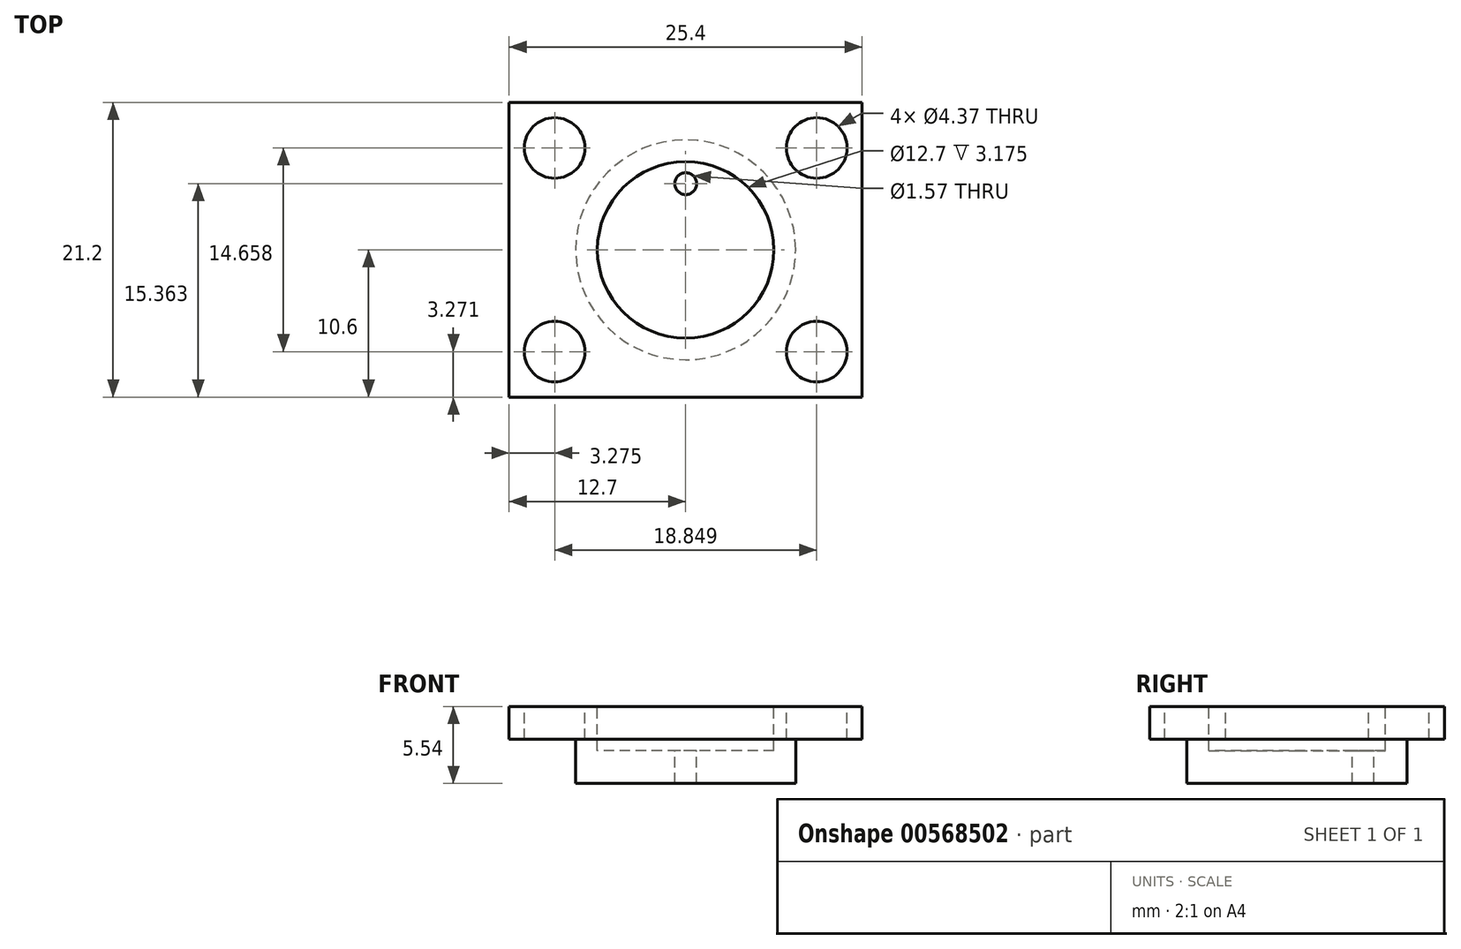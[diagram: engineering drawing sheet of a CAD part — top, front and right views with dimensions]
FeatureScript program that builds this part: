
annotation { "Feature Type Name" : "Feature", "Feature Type Description" : "" }
export const myFeature = defineFeature(function(context is Context, id is Id, definition is map)
    precondition{}
    {
        {
            var Q0;
            Q0=qCreatedBy(makeId("Top.planeOp"),FACE);
            var sketch = newSketch(context, id + "F0", { "sketchPlane" : qUnion([Q0])});
            skCircle(sketch, "E0", {"center": v(0, 0) * mm, "radius": 7.91 * mm});
            skSolve(sketch);
        }
        {
            var Q0;
            Q0 = qSketchRegion(id + "F0", true);
            extrude(context, id + "F1", {"entities" : qUnion([Q0]), "depth" : 3.17 * mm, "offsetDistance" : 25.4 * mm});
        }
        {
            var Q0;
            Q0=makeQuery(id+"F1.opExtrude","CAP_FACE",FACE,{"disambiguationData":[OSD([sQuery(id+"F0.wireOp",EDGE,"E0")])],"isStart":false});
            var sketch = newSketch(context, id + "F2", { "sketchPlane" : qUnion([Q0])});
            skLineSegment(sketch, "E1.bottom", {"start": v(-12.7, 10.6) * mm, "end": v(12.7, 10.6) * mm});
            skLineSegment(sketch, "E1.top", {"start": v(-12.7, -10.6) * mm, "end": v(12.7, -10.6) * mm});
            skLineSegment(sketch, "E1.left", {"start": v(-12.7, 10.6) * mm, "end": v(-12.7, -10.6) * mm});
            skLineSegment(sketch, "E1.right", {"start": v(12.7, 10.6) * mm, "end": v(12.7, -10.6) * mm});
            skPoint(sketch, "E1.middle", {"position": v(0, 0) * mm});
            skSolve(sketch);
        }
        {
            var Q0;
            Q0 = qSketchRegion(id + "F2", true);
            extrude(context, id + "F3", {"entities" : qUnion([Q0]), "operationType" : NewBodyOperationType.ADD, "depth" : 2.36 * mm, "offsetDistance" : 25.4 * mm});
        }
        {
            var Q0;
            Q0=makeQuery(id+"F3.opExtrude","CAP_FACE",FACE,{"disambiguationData":[OSD([sQuery(id+"F2.wireOp",EDGE,"E1.bottom"),sQuery(id+"F2.wireOp",EDGE,"E1.top"),sQuery(id+"F2.wireOp",EDGE,"E1.left"),sQuery(id+"F2.wireOp",EDGE,"E1.right")])],"isStart":false});
            var sketch = newSketch(context, id + "F4", { "sketchPlane" : qUnion([Q0])});
            skCircle(sketch, "E2", {"center": v(0, 0) * mm, "radius": 6.35 * mm});
            skSolve(sketch);
        }
        {
            var Q0;
            Q0 = qSketchRegion(id + "F4", true);
            extrude(context, id + "F5", {"entities" : qUnion([Q0]), "operationType" : NewBodyOperationType.REMOVE, "oppositeDirection" : true, "depth" : 3.17 * mm, "offsetDistance" : 25.4 * mm});
        }
        {
            var Q0;
            Q0=makeQuery(id+"F5.boolean.opBoolean","COPY",FACE,{"derivedFrom":makeQuery(id+"F5.opExtrude","CAP_FACE",FACE,{"disambiguationData":[OSD([sQuery(id+"F4.wireOp",EDGE,"E2")])],"isStart":false})});
            var sketch = newSketch(context, id + "F6", { "sketchPlane" : qUnion([Q0])});
            skLineSegment(sketch, "E3", {"start": v(0, 0) * mm, "end": v(0, 4.76) * mm});
            skCircle(sketch, "E4", {"center": v(0, 4.76) * mm, "radius": 0.79 * mm});
            skSolve(sketch);
        }
        {
            var Q0;
            Q0 = qSketchRegion(id + "F6", true);
            extrude(context, id + "F7", {"entities" : qUnion([Q0]), "operationType" : NewBodyOperationType.REMOVE, "endBound" : BoundingType.THROUGH_ALL, "oppositeDirection" : true, "depth" : 25.4 * mm, "offsetDistance" : 25.4 * mm});
        }
        {
            var Q0;
            Q0=makeQuery(id+"F3.opExtrude","CAP_FACE",FACE,{"disambiguationData":[OSD([sQuery(id+"F2.wireOp",EDGE,"E1.bottom"),sQuery(id+"F2.wireOp",EDGE,"E1.top"),sQuery(id+"F2.wireOp",EDGE,"E1.left"),sQuery(id+"F2.wireOp",EDGE,"E1.right")])],"isStart":false});
            var sketch = newSketch(context, id + "F8", { "sketchPlane" : qUnion([Q0])});
            skCircle(sketch, "E5", {"center": v(-9.42, 7.33) * mm, "radius": 2.18 * mm});
            skCircle(sketch, "E6.0.1.0", {"center": v(-9.42, -7.33) * mm, "radius": 2.18 * mm});
            skCircle(sketch, "E6.1.0.0", {"center": v(9.42, 7.33) * mm, "radius": 2.18 * mm});
            skCircle(sketch, "E6.1.1.0", {"center": v(9.42, -7.33) * mm, "radius": 2.18 * mm});
            skLineSegment(sketch, "E6.direction1", {"start": v(-9.42, 7.33) * mm, "end": v(9.42, 7.33) * mm, "construction": true});
            skLineSegment(sketch, "E6.direction2", {"start": v(-9.42, 7.33) * mm, "end": v(-9.42, -7.33) * mm, "construction": true});
            skLineSegment(sketch, "E7", {"start": v(-9.42, 7.33) * mm, "end": v(-12.7, 7.33) * mm});
            skPoint(sketch, "E8", {"position": v(-11.6, 7.33) * mm});
            skLineSegment(sketch, "E9", {"start": v(-9.42, -10.6) * mm, "end": v(-9.42, -7.33) * mm});
            skLineSegment(sketch, "E10", {"start": v(12.7, 7.33) * mm, "end": v(9.42, 7.33) * mm});
            skSolve(sketch);
        }
        {
            var Q0;
            Q0=makeQuery(id+"F8.imprint","IMPRINT",FACE,{"disambiguationData":[TD([[makeQuery(id+"F8.imprint","IMPRINT",EDGE,{"derivedFrom":sQuery(id+"F8.wireOp",EDGE,"E6.1.0.0")}),1.0]])]});
            var Q1;
            Q1=makeQuery(id+"F8.imprint","IMPRINT",FACE,{"disambiguationData":[TD([[makeQuery(id+"F8.imprint","IMPRINT",EDGE,{"derivedFrom":sQuery(id+"F8.wireOp",EDGE,"E5")}),1.0]])]});
            var Q2;
            Q2=makeQuery(id+"F8.imprint","IMPRINT",FACE,{"disambiguationData":[TD([[makeQuery(id+"F8.imprint","IMPRINT",EDGE,{"derivedFrom":sQuery(id+"F8.wireOp",EDGE,"E6.0.1.0")}),1.0]])]});
            var Q3;
            Q3=makeQuery(id+"F8.imprint","IMPRINT",FACE,{"disambiguationData":[TD([[makeQuery(id+"F8.imprint","IMPRINT",EDGE,{"derivedFrom":sQuery(id+"F8.wireOp",EDGE,"E6.1.1.0")}),1.0]])]});
            extrude(context, id + "F9", {"entities" : qUnion([Q0, Q1, Q2, Q3]), "operationType" : NewBodyOperationType.REMOVE, "endBound" : BoundingType.THROUGH_ALL, "oppositeDirection" : true, "depth" : 25.4 * mm, "offsetDistance" : 25.4 * mm});
        }
    });
